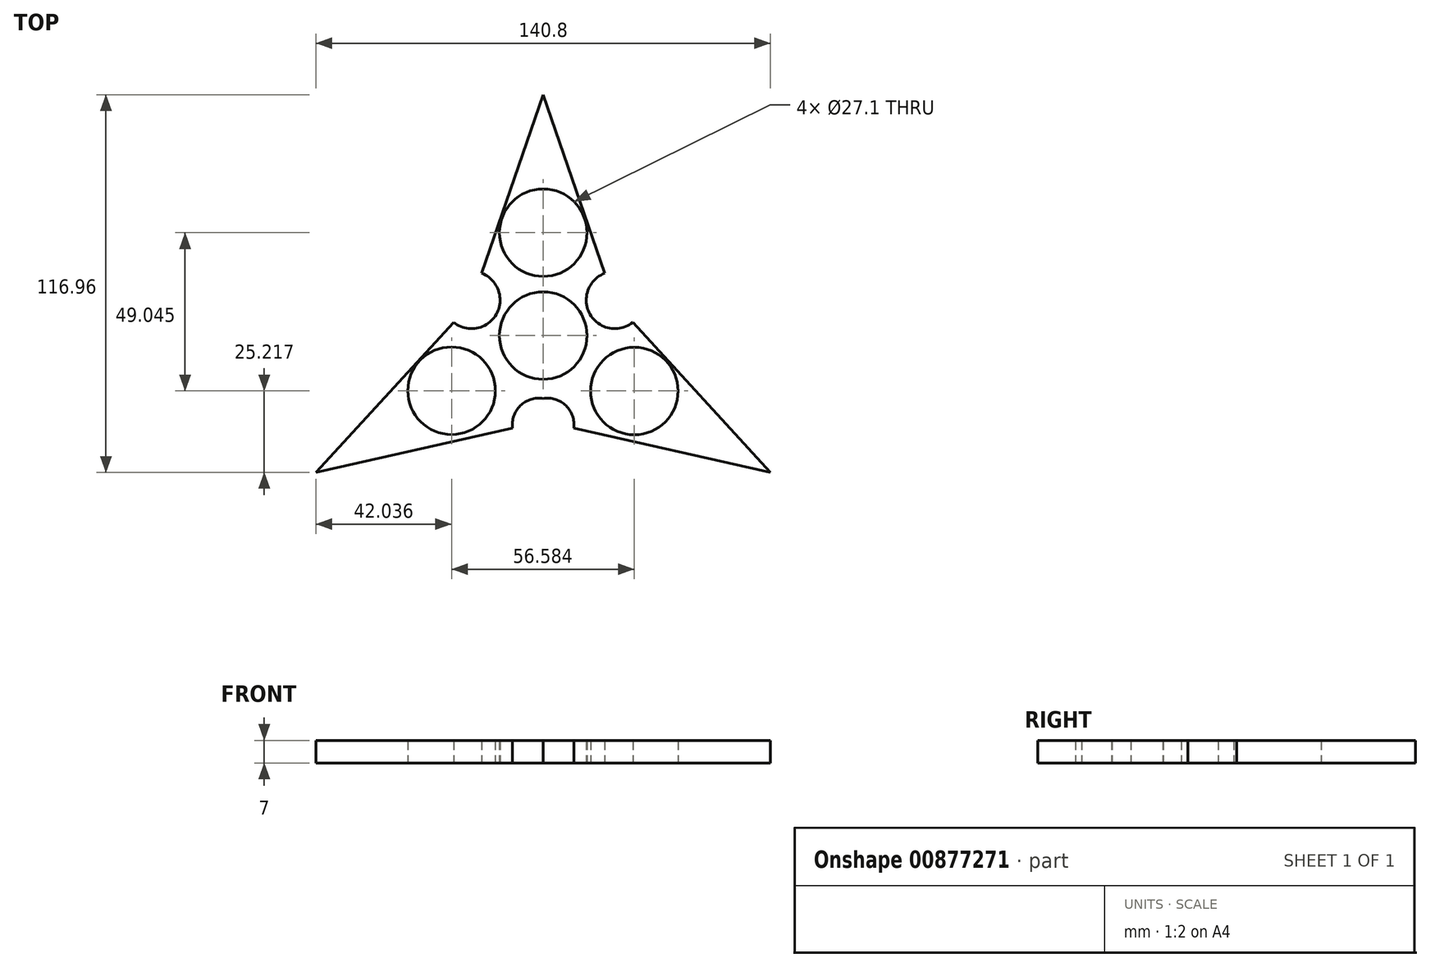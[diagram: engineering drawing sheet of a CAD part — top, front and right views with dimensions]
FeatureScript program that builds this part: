
annotation { "Feature Type Name" : "Feature", "Feature Type Description" : "" }
export const myFeature = defineFeature(function(context is Context, id is Id, definition is map)
    precondition{}
    {
        {
            var Q0;
            Q0=qCreatedBy(makeId("Top.planeOp"),FACE);
            var sketch = newSketch(context, id + "F0", { "sketchPlane" : qUnion([Q0])});
            skCircle(sketch, "E0", {"center": v(0, 0) * mm, "radius": 11.05 * mm});
            skCircle(sketch, "E1", {"center": v(0, 0) * mm, "radius": 13.55 * mm});
            skCircle(sketch, "E2", {"center": v(0, 31.87) * mm, "radius": 11.05 * mm});
            skCircle(sketch, "E3", {"center": v(0, 31.87) * mm, "radius": 13.55 * mm});
            skCircle(sketch, "E4.1.0", {"center": v(-28.36, -17.1) * mm, "radius": 11.05 * mm});
            skCircle(sketch, "E4.1.1", {"center": v(-28.36, -17.1) * mm, "radius": 13.55 * mm});
            skCircle(sketch, "E4.2.0", {"center": v(28.22, -17.17) * mm, "radius": 11.05 * mm});
            skCircle(sketch, "E4.2.1", {"center": v(28.22, -17.17) * mm, "radius": 13.55 * mm});
            skPoint(sketch, "E4.center", {"position": v(-0.05, -0.8) * mm});
            skArc(sketch, "E5", {"start": v(-27.75, 4.08) * mm, "mid": v(-14.53, 6.6) * mm, "end": v(-19, 19.3) * mm});
            skArc(sketch, "E6", {"start": v(0, -19.5) * mm, "mid": v(-7.06, -21.72) * mm, "end": v(-9.48, -28.72) * mm});
            skArc(sketch, "E7.MirrorCS", {"start": v(27.75, 4.08) * mm, "mid": v(14.53, 6.6) * mm, "end": v(19, 19.3) * mm});
            skArc(sketch, "E8.MirrorCS", {"start": v(0, -19.5) * mm, "mid": v(7.06, -21.72) * mm, "end": v(9.48, -28.72) * mm});
            skLineSegment(sketch, "E9", {"start": v(-70.4, -42.4) * mm, "end": v(-9.48, -28.72) * mm});
            skLineSegment(sketch, "E10", {"start": v(-70.4, -42.4) * mm, "end": v(-27.75, 4.08) * mm});
            skLineSegment(sketch, "E11", {"start": v(-19, 19.3) * mm, "end": v(0, 74.57) * mm});
            skLineSegment(sketch, "E12.MirrorCS", {"start": v(70.4, -42.4) * mm, "end": v(9.48, -28.72) * mm});
            skLineSegment(sketch, "E13.MirrorCS", {"start": v(19, 19.3) * mm, "end": v(0, 74.57) * mm});
            skLineSegment(sketch, "E14.MirrorCS", {"start": v(70.4, -42.4) * mm, "end": v(27.75, 4.08) * mm});
            skSolve(sketch);
        }
        {
            var Q0;
            Q0 = qSketchRegion(id + "F0", true);
            extrude(context, id + "F1", {"entities" : qUnion([Q0]), "depth" : 7 * mm, "offsetDistance" : 25 * mm});
        }
    });
